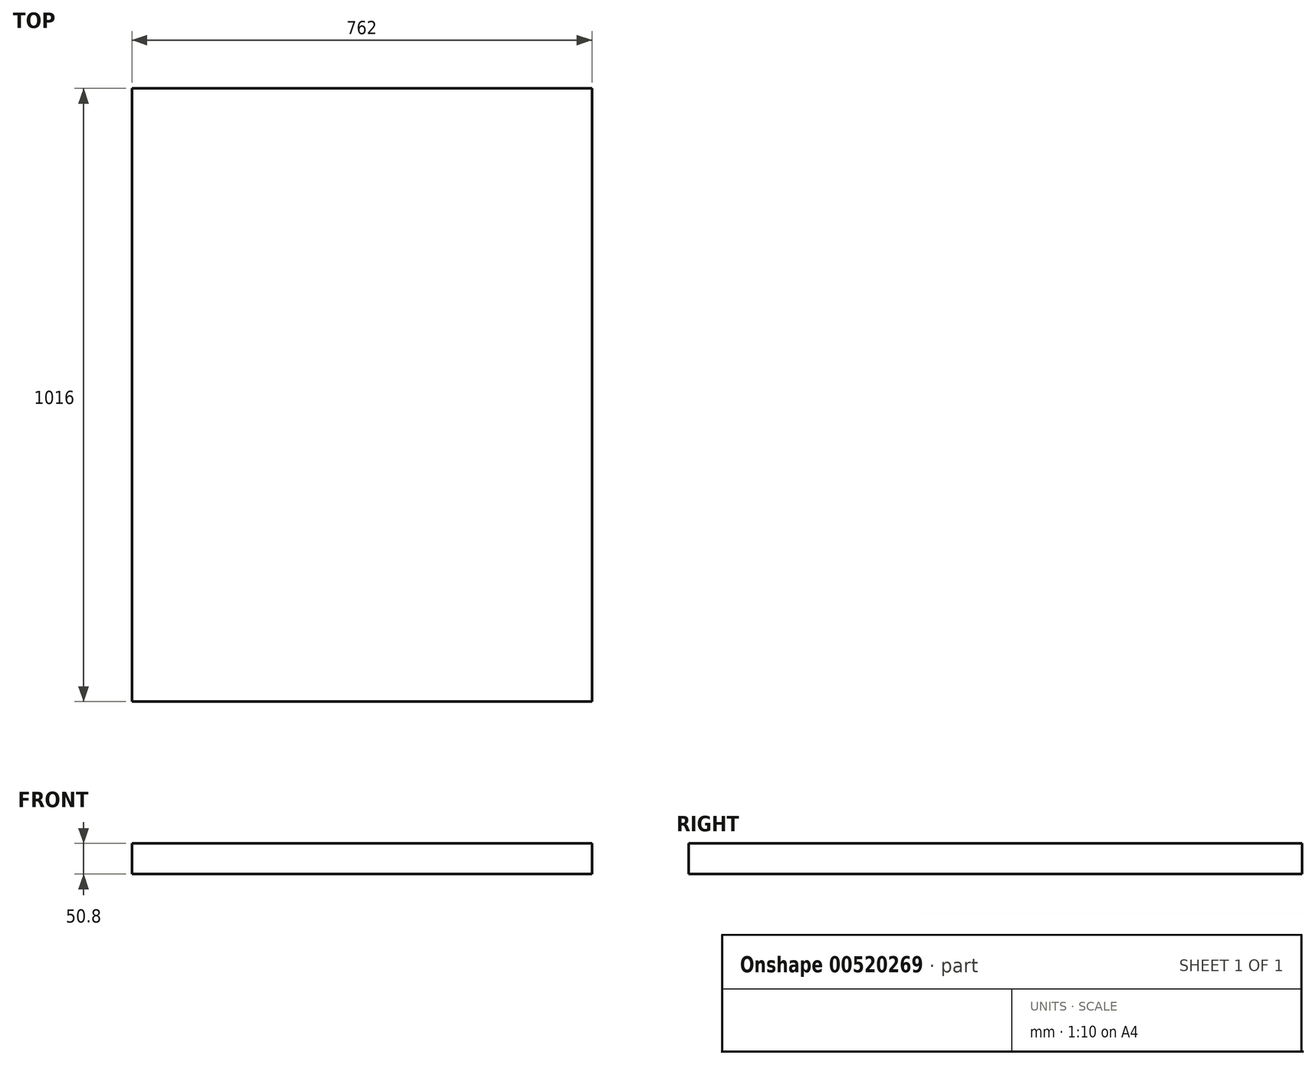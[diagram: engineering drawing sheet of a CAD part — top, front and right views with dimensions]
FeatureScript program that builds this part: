
annotation { "Feature Type Name" : "Feature", "Feature Type Description" : "" }
export const myFeature = defineFeature(function(context is Context, id is Id, definition is map)
    precondition{}
    {
        {
            var Q0;
            Q0=qCreatedBy(makeId("Top.planeOp"),FACE);
            var sketch = newSketch(context, id + "F0", { "sketchPlane" : qUnion([Q0])});
            skLineSegment(sketch, "E0.bottom", {"start": v(-381, 508) * mm, "end": v(381, 508) * mm});
            skLineSegment(sketch, "E0.top", {"start": v(-381, -508) * mm, "end": v(381, -508) * mm});
            skLineSegment(sketch, "E0.left", {"start": v(-381, 508) * mm, "end": v(-381, -508) * mm});
            skLineSegment(sketch, "E0.right", {"start": v(381, 508) * mm, "end": v(381, -508) * mm});
            skPoint(sketch, "E0.middle", {"position": v(0, 0) * mm});
            skSolve(sketch);
        }
        {
            var Q0;
            Q0 = qSketchRegion(id + "F0", true);
            extrude(context, id + "F1", {"entities" : qUnion([Q0]), "depth" : 50.8 * mm, "offsetDistance" : 25.4 * mm});
        }
    });
